# Revit family: No interlocked sockets 380_415 V
name_source: partatom
category: Installations électriques
revit_build: Autodesk Revit 2018 (Build: 20170223_1515(x64)
units: mm (PartAtom-declared; Revit-internal decimal feet)

## family parameters
Conserver l'orientation des annotations = Non
Cote de connecteur circulaire = Utiliser le diamètre
Couper avec des vides une fois chargée = Non
Hôte = Face
Partagée = Non
Point de calcul de pièce = Non
Type d'élément = Normal

## types (21) — shared parameters
Elévation par défaut = 1000 mm  [stored 3.28084 ft]
Fabricant = Legrand
International standard socket for flush mounting or surface mounting with accessory allows the connection of power devices = International standard socket for flush mounting or surface mounting with accessory allows the connection of power devices
Maximum use temperature = 40
Minimum use temperature = -25
Position of earth h = 6
Product family = 0854-P17 TEMPRA PRO
Standard IEC or NFC = IEC
Tension V = 400 V  50/60 Hz red
characteristic color = red
connecting type = screw terminals
material of box = plastic
resistance to chocks IK = 9

## per-type parameters (varying)
| type | Description | Flush E or Surface mounting S | Minimum installation temperature | Number of poles | depth for flush mounting mm | depth mm | halogen free | height mm | horizontal fixing distance mm | intensity A | protection class IP | vertical fixing distance mm | width mm |
| P17 Pro - IP66/67 - 63 A - 3P+N+E | LG-555589_Panel mounting socket P17 Pro - IP66/67 - 380/415 V - 63 A - 3P+N+E | flush mounting | -5 | 5 | 84 mm  [stored 0.275591 ft] | 161 mm  [stored 0.528215 ft] | Non | 106 mm  [stored 0.347769 ft] | 77 mm  [stored 0.252625 ft] | 63 A |  | 85 mm | 106 mm  [stored 0.347769 ft] |
| P17 Pro - IP66/67 - 63 A - 3P+E | LG-555588_Panel mounting socket P17 Pro - IP66/67 - 380/415 V - 63 A - 3P+E | flush mounting | -5 | 4 | 84 mm  [stored 0.275591 ft] | 161 mm  [stored 0.528215 ft] | Non | 106 mm  [stored 0.347769 ft] | 77 mm  [stored 0.252625 ft] | 63 A |  | 85 mm | 106 mm  [stored 0.347769 ft] |
| P17 Pro - IP66/67 - 125 A - 3P+N+E | LG-555689_Panel mounting socket P17 Pro - IP66/67 - 380/415 V - 125 A - 3P+N+E | flush mounting | -5 | 5 | 89 mm  [stored 0.291995 ft] | 182 mm  [stored 0.597113 ft] | Non | 146 mm  [stored 0.479003 ft] | 124 mm | 125 A |  | 124 mm | 146 mm  [stored 0.479003 ft] |
| P17 Pro - IP66/67 - 125 A - 3P+E | LG-555688_Panel mounting socket P17 Pro - IP66/67 - 380/415 V - 125 A - 3P+E | flush mounting | -5 | 4 | 89 mm  [stored 0.291995 ft] | 182 mm  [stored 0.597113 ft] | Non | 146 mm  [stored 0.479003 ft] | 124 mm | 125 A |  | 124 mm | 146 mm  [stored 0.479003 ft] |
| P17 - IP66/67 - 32 A - 3P+N+E | LG-555489_Panel mounting socket P17 - IP66/67 - 380/415 V - 32 A - 3P+N+E | flush and surface mounting | -5 | 5 | 43 mm  [stored 0.141076 ft] | 94 mm  [stored 0.308399 ft] | Non | 84 mm  [stored 0.275591 ft] | 70 mm  [stored 0.229659 ft] | 32 A |  | 70 mm  [stored 0.229659 ft] | 84 mm  [stored 0.275591 ft] |
| P17 - IP66/67 - 32 A - 3P+E | LG-555488_Panel mounting socket P17 - IP66/67 - 380/415 V - 32 A - 3P+E | flush and surface mounting | -5 | 4 | 42 mm | 92 mm | Non | 84 mm  [stored 0.275591 ft] | 70 mm  [stored 0.229659 ft] | 32 A |  | 70 mm  [stored 0.229659 ft] | 84 mm  [stored 0.275591 ft] |
| P17 - IP66/67 - 16 A - 3P+N+E | LG-555389_Panel mounting socket P17 - IP66/67 - 380/415 V - 16 A - 3P+N+E | flush and surface mounting | -5 | 5 | 37 mm  [stored 0.121391 ft] | 81 mm | Non | 84 mm  [stored 0.275591 ft] | 70 mm  [stored 0.229659 ft] | 16 A |  | 70 mm  [stored 0.229659 ft] | 84 mm  [stored 0.275591 ft] |
| P17 - IP66/67 - 16 A - 3P+E | LG-555388_Panel mounting socket P17 - IP66/67 - 380/415 V - 16 A - 3P+E | flush and surface mounting | -5 | 4 | 36 mm | 79 mm | Non | 84 mm  [stored 0.275591 ft] | 70 mm  [stored 0.229659 ft] | 16 A |  | 70 mm  [stored 0.229659 ft] | 84 mm  [stored 0.275591 ft] |
| P17 - 32A - 3P+E - IP1 | LG-555290_Panel mounting socket  P17  32A 3P+E 440/460V IP44 | flush and surface mounting | -5 | 4 | 42 mm | 87 mm | Oui | 84 mm  [stored 0.275591 ft] | 70 mm  [stored 0.229659 ft] | 32 A | IP44 | 70 mm  [stored 0.229659 ft] | 84 mm  [stored 0.275591 ft] |
| P17 - IP44 - 32 A - 3P+N+E | LG-555289_Panel mounting socket P17 - inclined outlet - IP44 - 380/415 V - 32 A - 3P+N+E | flush and surface mounting | -5 | 5 | 43 mm  [stored 0.141076 ft] | 89 mm  [stored 0.291995 ft] | Oui | 84 mm  [stored 0.275591 ft] | 70 mm  [stored 0.229659 ft] | 32 A | IP44 | 70 mm  [stored 0.229659 ft] | 84 mm  [stored 0.275591 ft] |
| P17 - IP44 - 32 A - 3P+E | LG-555288_Panel mounting socket P17 - inclined outlet - IP44 - 380/415 V - 32 A - 3P+E | flush and surface mounting | -5 | 4 | 42 mm | 87 mm | Oui | 84 mm  [stored 0.275591 ft] | 70 mm  [stored 0.229659 ft] | 32 A | IP44 | 70 mm  [stored 0.229659 ft] | 84 mm  [stored 0.275591 ft] |
| P17 - IP44 - 16A - 3P+N+E 1 | LG-555189_Panel mounting socket P17 - inclined outlet - IP44 - 380/415 V - 16 A - 3P+N+E | flush and surface mounting | -5 | 5 | 37 mm  [stored 0.121391 ft] | 76 mm | Oui | 84 mm  [stored 0.275591 ft] | 70 mm  [stored 0.229659 ft] | 16 A | IP44 | 70 mm  [stored 0.229659 ft] | 84 mm  [stored 0.275591 ft] |
| P17 - IP44 - 16A - 3P+E 1 | LG-555188_Panel mounting socket P17 - inclined outlet - IP44 - 380/415 V - 16 A - 3P+E | flush and surface mounting | -5 | 4 | 36 mm | 74 mm  [stored 0.242782 ft] | Oui | 84 mm  [stored 0.275591 ft] | 70 mm  [stored 0.229659 ft] | 16 A | IP44 | 70 mm  [stored 0.229659 ft] | 84 mm  [stored 0.275591 ft] |
| P17 - 32A - 4P+E - IP44 | LG-090166_Panel mounting socket P17  32A 4P+E 380/415V IP44 | flush and surface mounting | -5 | 5 | 43 mm  [stored 0.141076 ft] | 89 mm  [stored 0.291995 ft] | Oui | 84 mm  [stored 0.275591 ft] | 70 mm  [stored 0.229659 ft] | 32 A | IP44 | 70 mm  [stored 0.229659 ft] | 84 mm  [stored 0.275591 ft] |
| P17 - 32A - 3P+E - IP44 | LG-090165_Panel mounting socket P17  32A 3P+E 380/415V IP44 | flush and surface mounting | -5 | 4 | 42 mm | 87 mm | Oui | 84 mm  [stored 0.275591 ft] | 70 mm  [stored 0.229659 ft] | 32 A | IP44 | 70 mm  [stored 0.229659 ft] | 84 mm  [stored 0.275591 ft] |
| P17 - 16A - 4P+E - IP44 | LG-090164_Panel mounting socket P17 16A 4P+E 380/415V IP44 | flush and surface mounting | -5 | 5 | 37 mm  [stored 0.121391 ft] | 76 mm | Oui | 84 mm  [stored 0.275591 ft] | 70 mm  [stored 0.229659 ft] | 16 A | IP44 | 70 mm  [stored 0.229659 ft] | 84 mm  [stored 0.275591 ft] |
| P17 - 16A - 3P+E - IP44 | LG-090163_Panel mounting sockets P17  16A 3P+E 380/415V IP44 | flush and surface mounting | -5 | 4 | 36 mm | 74 mm  [stored 0.242782 ft] | Oui | 84 mm  [stored 0.275591 ft] | 70 mm  [stored 0.229659 ft] | 16 A | IP44 | 70 mm  [stored 0.229659 ft] | 84 mm  [stored 0.275591 ft] |
| P17 - IP44 - 32A - 3P+N+E | LG-058059_Panel mounting sockets P17  - IP44 - straight outlet - 380/415 V - 32 A -3P+N+E | flush mounting |  | 4 | 31 mm | 93 mm | Oui | 105 mm | 60 mm  [stored 0.19685 ft] | 32 A | IP44 | 60 mm  [stored 0.19685 ft] | 77 mm  [stored 0.252625 ft] |
| P17    IP44  32 A  3P+E | LG-058058_Panel mounting sockets P17  - IP44 - straight outlet - 380/415 V - 32 A -3P+E | flush mounting |  | 3 | 31 mm | 93 mm | Oui | 98 mm | 60 mm  [stored 0.19685 ft] | 32 A | IP44 | 60 mm  [stored 0.19685 ft] | 75 mm |
| P17 - IP44 - 16A - 3P+N+E | LG-057359_Panel mounting sockets P17 IP44 - 380/415 V - 16 A - 3P+N+E | flush mounting |  | 4 | 22 mm  [stored 0.0721785 ft] | 73 mm | Oui | 94 mm  [stored 0.308399 ft] | 52 mm | 16 A | IP44 | 52 mm | 70 mm  [stored 0.229659 ft] |
| P17 - IP44 - 16A - 3P+E | LG-057358_Panel mounting sockets P17 IP44 - 380/415 V - 16 A - 3P+E | flush mounting |  | 3 | 22 mm  [stored 0.0721785 ft] | 73 mm | Oui | 86 mm | 52 mm | 16 A | IP44 | 52 mm | 65 mm  [stored 0.213255 ft] |

note: [stored X ft] marks values corroborated as IEEE doubles in the binary element streams (Revit-internal decimal feet)
